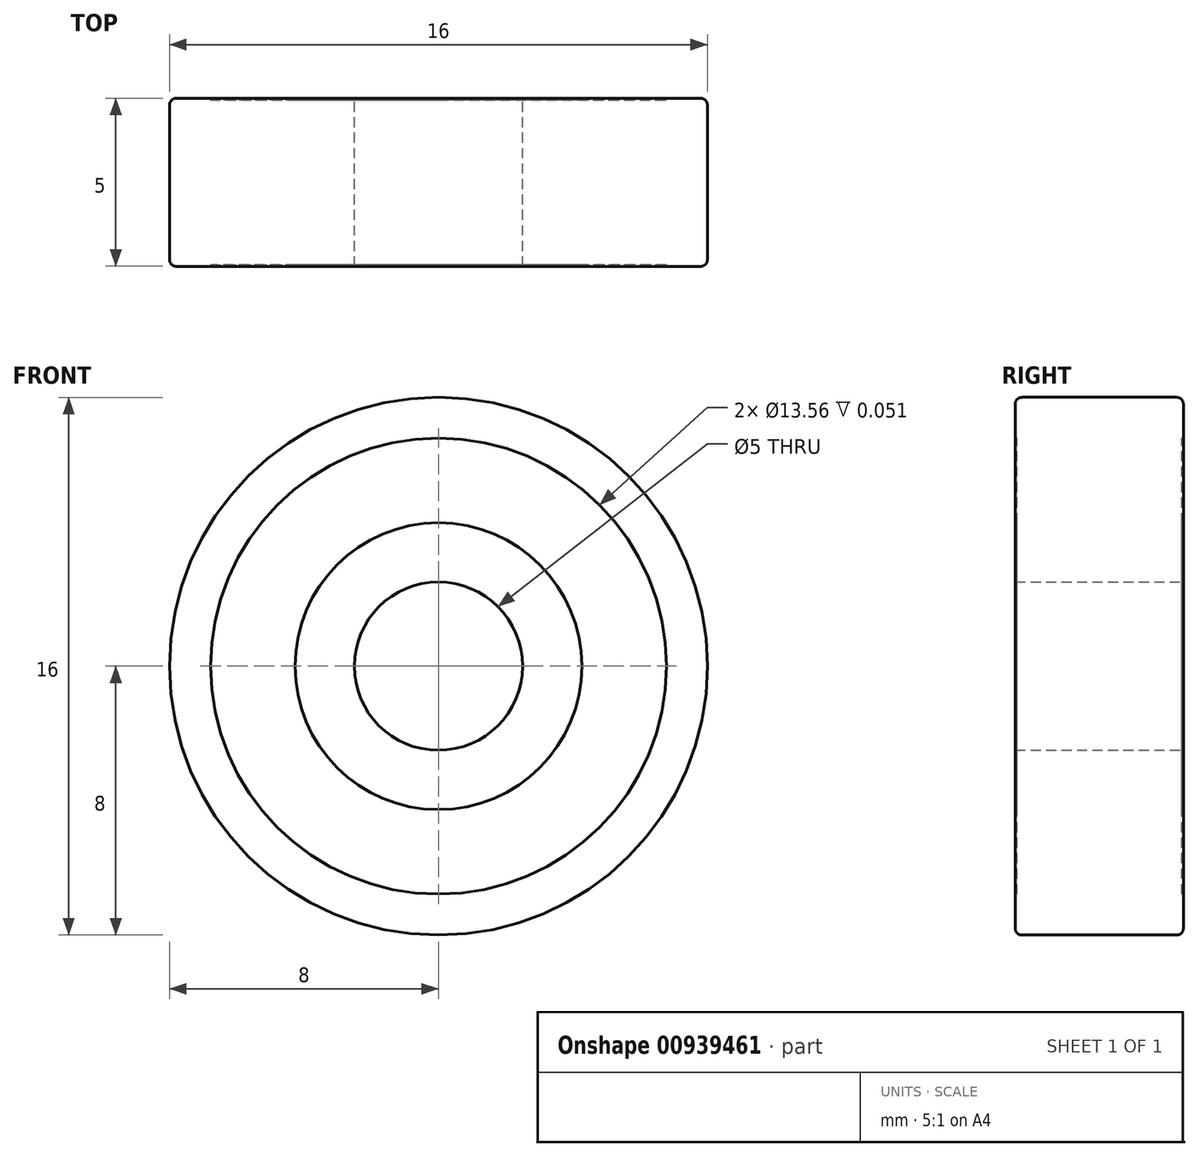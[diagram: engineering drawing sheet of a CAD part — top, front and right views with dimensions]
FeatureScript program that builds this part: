
annotation { "Feature Type Name" : "Feature", "Feature Type Description" : "" }
export const myFeature = defineFeature(function(context is Context, id is Id, definition is map)
    precondition{}
    {
        {
            var Q0;
            Q0=qCreatedBy(makeId("Front.planeOp"),FACE);
            var sketch = newSketch(context, id + "F0", { "sketchPlane" : qUnion([Q0])});
            skCircle(sketch, "E0", {"center": v(0, 0) * mm, "radius": 8 * mm});
            skCircle(sketch, "E1", {"center": v(0, 0) * mm, "radius": 2.5 * mm});
            skSolve(sketch);
        }
        {
            var Q0;
            Q0=qSketchRegion(id+"F0",true);
            extrude(context, id + "F1", {"entities" : qUnion([Q0]), "depth" : 5 * mm});
        }
        {
            var Q0;
            Q0=qCreatedBy(makeId("Front.planeOp"),FACE);
            var sketch = newSketch(context, id + "F2", { "sketchPlane" : qUnion([Q0])});
            skCircle(sketch, "E2", {"center": v(0, 0) * mm, "radius": 4.27 * mm});
            skCircle(sketch, "E3", {"center": v(0, 0) * mm, "radius": 6.78 * mm});
            skSolve(sketch);
        }
        {
            var Q0;
            Q0=makeQuery(id+"F2.imprint","IMPRINT",FACE,{"disambiguationData":[TD([[makeQuery(id+"F2.imprint","IMPRINT",EDGE,{"derivedFrom":sQuery(id+"F2.wireOp",EDGE,"E2")}),-1.0]])]});
            var Q1;
            Q1=makeQuery(id+"F1.opExtrude","CAP_FACE",FACE,{"disambiguationData":[OSD([sQuery(id+"F0.wireOp",EDGE,"E0"),sQuery(id+"F0.wireOp",EDGE,"E1")])],"isStart":false});
            extrude(context, id + "F3", {"entities" : qUnion([Q0, Q1]), "operationType" : NewBodyOperationType.REMOVE, "depth" : 0.05 * mm});
        }
        {
            var Q0;
            Q0=makeQuery(id+"F1.opExtrude","CAP_FACE",FACE,{"disambiguationData":[OSD([sQuery(id+"F0.wireOp",EDGE,"E0"),sQuery(id+"F0.wireOp",EDGE,"E1")])],"isStart":false});
            var sketch = newSketch(context, id + "F4", { "sketchPlane" : qUnion([Q0])});
            skCircle(sketch, "E4", {"center": v(0, 0) * mm, "radius": 4.27 * mm});
            skCircle(sketch, "E5", {"center": v(0, 0) * mm, "radius": 6.78 * mm});
            skSolve(sketch);
        }
        {
            var Q0;
            Q0=makeQuery(id+"F4.imprint","IMPRINT",FACE,{"disambiguationData":[TD([[makeQuery(id+"F4.imprint","IMPRINT",EDGE,{"derivedFrom":sQuery(id+"F4.wireOp",EDGE,"E4")}),-1.0]])]});
            extrude(context, id + "F5", {"entities" : qUnion([Q0]), "operationType" : NewBodyOperationType.REMOVE, "oppositeDirection" : true, "depth" : 0.05 * mm});
        }
        {
            var Q0;
            Q0=makeQuery(id+"F1.opExtrude","CAP_EDGE",EDGE,{"disambiguationData":[OSD([sQuery(id+"F0.wireOp",EDGE,"E0")])],"isStart":false});
            var Q1;
            Q1=makeQuery(id+"F1.opExtrude","CAP_EDGE",EDGE,{"disambiguationData":[OSD([sQuery(id+"F0.wireOp",EDGE,"E0")])],"isStart":true});
            fillet(context, id + "F6", {"entities" : qUnion([Q0, Q1]), "radius" : 0.2 * mm, "tangentPropagation" : true, "allowEdgeOverflow" : false});
        }
    });
